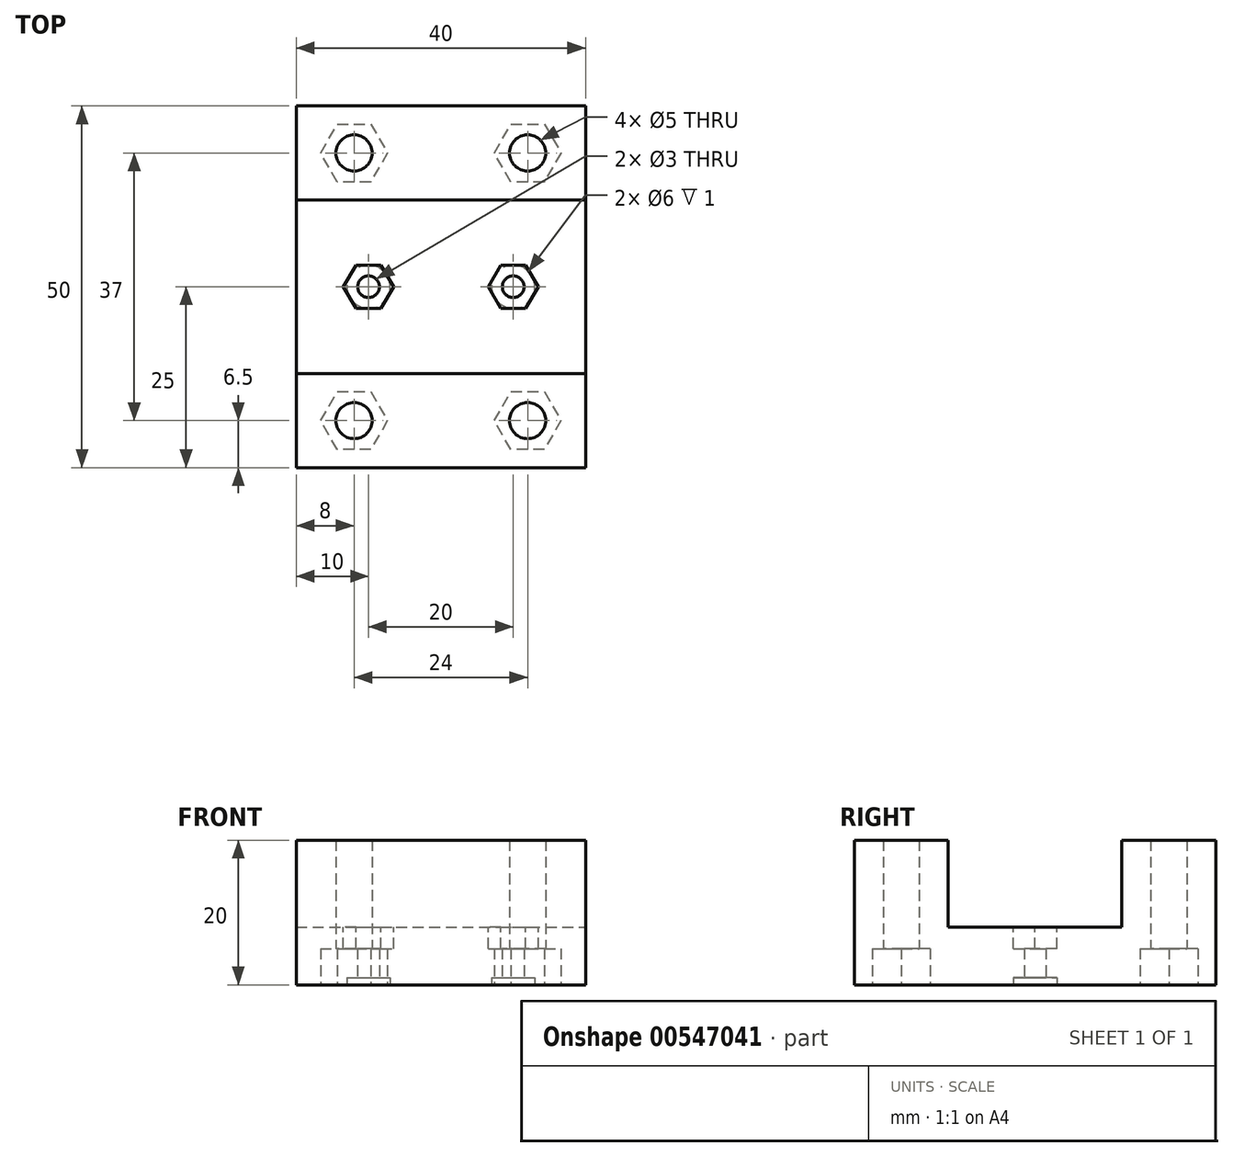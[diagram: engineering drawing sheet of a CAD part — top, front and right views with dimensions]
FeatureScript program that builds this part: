
annotation { "Feature Type Name" : "Feature", "Feature Type Description" : "" }
export const myFeature = defineFeature(function(context is Context, id is Id, definition is map)
    precondition{}
    {
        {
            var Q0;
            Q0=qCreatedBy(makeId("Top.planeOp"),FACE);
            var sketch = newSketch(context, id + "F0", { "sketchPlane" : qUnion([Q0])});
            skLineSegment(sketch, "E0.bottom", {"start": v(-40, 50) * mm, "end": v(0, 50) * mm});
            skLineSegment(sketch, "E0.top", {"start": v(-40, 0) * mm, "end": v(0, 0) * mm});
            skLineSegment(sketch, "E0.left", {"start": v(-40, 50) * mm, "end": v(-40, 0) * mm});
            skLineSegment(sketch, "E0.right", {"start": v(0, 50) * mm, "end": v(0, 0) * mm});
            skLineSegment(sketch, "E1", {"start": v(-40, 37) * mm, "end": v(0, 37) * mm});
            skLineSegment(sketch, "E2", {"start": v(-40, 13) * mm, "end": v(0, 13) * mm});
            skPoint(sketch, "E3", {"position": v(-8, 6.5) * mm});
            skPoint(sketch, "E4", {"position": v(-32, 43.5) * mm});
            skPoint(sketch, "E5", {"position": v(-32, 6.5) * mm});
            skPoint(sketch, "E6", {"position": v(-8, 43.5) * mm});
            skSolve(sketch);
        }
        {
            var Q0;
            {var subQ0=sQuery(id+"F0.wireOp",EDGE,"E1");Q0=makeQuery(id+"F0.imprint","IMPRINT",FACE,{"disambiguationData":[TD([[makeQuery(id+"F0.imprint","IMPRINT",EDGE,{"derivedFrom":subQ0}),-1.0]])]});}
            extrude(context, id + "F1", {"entities" : qUnion([Q0]), "depth" : 8 * mm, "offsetDistance" : 25 * mm});
        }
        {
            var Q0;
            {var subQ0=sQuery(id+"F0.wireOp",EDGE,"E0.bottom");Q0=makeQuery(id+"F0.imprint","IMPRINT",FACE,{"disambiguationData":[TD([[makeQuery(id+"F0.imprint","IMPRINT",EDGE,{"derivedFrom":subQ0}),-1.0]])]});}
            var Q1;
            {var subQ0=sQuery(id+"F0.wireOp",EDGE,"E0.top");Q1=makeQuery(id+"F0.imprint","IMPRINT",FACE,{"disambiguationData":[TD([[makeQuery(id+"F0.imprint","IMPRINT",EDGE,{"derivedFrom":subQ0}),1.0]])]});}
            extrude(context, id + "F2", {"entities" : qUnion([Q0, Q1]), "operationType" : NewBodyOperationType.ADD, "depth" : 20 * mm, "offsetDistance" : 25 * mm});
        }
        {
            var Q0;
            Q0=sQuery(id+"F0.wireOp",VERTEX,"E6");
            var Q1;
            Q1=sQuery(id+"F0.wireOp",VERTEX,"E4");
            var Q2;
            Q2=sQuery(id+"F0.wireOp",VERTEX,"E5");
            var Q3;
            Q3=sQuery(id+"F0.wireOp",VERTEX,"E3");
            var Q4;
            Q4=makeQuery(id+"F1.opExtrude","SWEPT_BODY",BODY,{"disambiguationData":[OSD([sQuery(id+"F0.wireOp",EDGE,"E0.left"),sQuery(id+"F0.wireOp",EDGE,"E0.right"),sQuery(id+"F0.wireOp",EDGE,"E1"),sQuery(id+"F0.wireOp",EDGE,"E2")])]});
            hole(context, id + "F3", {"style" : HoleStyle.SIMPLE, "endStyle" : HoleEndStyle.THROUGH, "oppositeDirection" : true, "holeDiameter" : 5 * mm, "isTappedThrough" : true, "tappedDepth" : 12 * mm, "tapClearance" : 3, "startFromSketch" : true, "locations" : qUnion([Q0, Q1, Q2, Q3]), "scope" : qUnion([Q4])});
        }
        {
            var Q0;
            {var subQ0=sQuery(id+"F0.wireOp",EDGE,"E0.top");Q0=makeQuery(id+"F0.imprint","IMPRINT",FACE,{"disambiguationData":[TD([[makeQuery(id+"F0.imprint","IMPRINT",EDGE,{"derivedFrom":subQ0}),1.0]])]});}
            var sketch = newSketch(context, id + "F4", { "sketchPlane" : qUnion([Q0])});
            skLineSegment(sketch, "E7", {"start": v(-10.3, 47.5) * mm, "end": v(-5.7, 47.5) * mm});
            skLineSegment(sketch, "E8", {"start": v(-5.7, 47.5) * mm, "end": v(-3.38, 43.5) * mm});
            skLineSegment(sketch, "E9", {"start": v(-3.38, 43.5) * mm, "end": v(-5.7, 39.5) * mm});
            skLineSegment(sketch, "E10", {"start": v(-5.7, 39.5) * mm, "end": v(-10.3, 39.5) * mm});
            skLineSegment(sketch, "E11", {"start": v(-10.3, 39.5) * mm, "end": v(-12.62, 43.5) * mm});
            skLineSegment(sketch, "E12", {"start": v(-12.62, 43.5) * mm, "end": v(-10.3, 47.5) * mm});
            skCircle(sketch, "E13", {"center": v(-8, 43.5) * mm, "radius": 4.62 * mm});
            skLineSegment(sketch, "E14", {"start": v(-10.3, 10.5) * mm, "end": v(-5.7, 10.5) * mm});
            skLineSegment(sketch, "E15", {"start": v(-5.7, 10.5) * mm, "end": v(-3.38, 6.5) * mm});
            skLineSegment(sketch, "E16", {"start": v(-3.38, 6.5) * mm, "end": v(-5.7, 2.5) * mm});
            skLineSegment(sketch, "E17", {"start": v(-5.7, 2.5) * mm, "end": v(-10.3, 2.5) * mm});
            skLineSegment(sketch, "E18", {"start": v(-10.3, 2.5) * mm, "end": v(-12.62, 6.5) * mm});
            skLineSegment(sketch, "E19", {"start": v(-12.62, 6.5) * mm, "end": v(-10.3, 10.5) * mm});
            skCircle(sketch, "E20", {"center": v(-8, 6.5) * mm, "radius": 4.62 * mm});
            skLineSegment(sketch, "E21", {"start": v(-34.3, 10.5) * mm, "end": v(-29.7, 10.5) * mm});
            skLineSegment(sketch, "E22", {"start": v(-29.7, 10.5) * mm, "end": v(-27.38, 6.5) * mm});
            skLineSegment(sketch, "E23", {"start": v(-27.38, 6.5) * mm, "end": v(-29.7, 2.5) * mm});
            skLineSegment(sketch, "E24", {"start": v(-29.7, 2.5) * mm, "end": v(-34.3, 2.5) * mm});
            skLineSegment(sketch, "E25", {"start": v(-34.3, 2.5) * mm, "end": v(-36.62, 6.5) * mm});
            skLineSegment(sketch, "E26", {"start": v(-36.62, 6.5) * mm, "end": v(-34.3, 10.5) * mm});
            skCircle(sketch, "E27", {"center": v(-32, 6.5) * mm, "radius": 4.62 * mm});
            skLineSegment(sketch, "E28", {"start": v(-34.3, 47.5) * mm, "end": v(-29.7, 47.5) * mm});
            skLineSegment(sketch, "E29", {"start": v(-29.7, 47.5) * mm, "end": v(-27.38, 43.5) * mm});
            skLineSegment(sketch, "E30", {"start": v(-27.38, 43.5) * mm, "end": v(-29.7, 39.5) * mm});
            skLineSegment(sketch, "E31", {"start": v(-29.7, 39.5) * mm, "end": v(-34.3, 39.5) * mm});
            skLineSegment(sketch, "E32", {"start": v(-34.3, 39.5) * mm, "end": v(-36.62, 43.5) * mm});
            skLineSegment(sketch, "E33", {"start": v(-36.62, 43.5) * mm, "end": v(-34.3, 47.5) * mm});
            skCircle(sketch, "E34", {"center": v(-32, 43.5) * mm, "radius": 4.62 * mm});
            skSolve(sketch);
        }
        {
            var Q0;
            Q0=makeQuery(id+"F4.imprint","IMPRINT",FACE,{"disambiguationData":[TD([[makeQuery(id+"F4.imprint","IMPRINT",EDGE,{"derivedFrom":sQuery(id+"F4.wireOp",EDGE,"E21")}),-1.0]])]});
            var Q1;
            Q1=makeQuery(id+"F4.imprint","IMPRINT",FACE,{"disambiguationData":[TD([[makeQuery(id+"F4.imprint","IMPRINT",EDGE,{"derivedFrom":sQuery(id+"F4.wireOp",EDGE,"E14")}),-1.0]])]});
            var Q2;
            Q2=makeQuery(id+"F4.imprint","IMPRINT",FACE,{"disambiguationData":[TD([[makeQuery(id+"F4.imprint","IMPRINT",EDGE,{"derivedFrom":sQuery(id+"F4.wireOp",EDGE,"E7")}),-1.0]])]});
            var Q3;
            Q3=makeQuery(id+"F4.imprint","IMPRINT",FACE,{"disambiguationData":[TD([[makeQuery(id+"F4.imprint","IMPRINT",EDGE,{"derivedFrom":sQuery(id+"F4.wireOp",EDGE,"E28")}),-1.0]])]});
            extrude(context, id + "F5", {"entities" : qUnion([Q0, Q1, Q2, Q3]), "operationType" : NewBodyOperationType.REMOVE, "depth" : 5 * mm, "offsetDistance" : 25 * mm});
        }
        {
            var Q0;
            {var subQ0=sQuery(id+"F0.wireOp",EDGE,"E1");Q0=makeQuery(id+"F0.imprint","IMPRINT",FACE,{"disambiguationData":[TD([[makeQuery(id+"F0.imprint","IMPRINT",EDGE,{"derivedFrom":subQ0}),-1.0]])]});}
            var sketch = newSketch(context, id + "F6", { "sketchPlane" : qUnion([Q0])});
            skPoint(sketch, "E35", {"position": v(-30, 25) * mm});
            skPoint(sketch, "E36", {"position": v(-10, 25) * mm});
            skSolve(sketch);
        }
        {
            var Q0;
            Q0=sQuery(id+"F6.wireOp",VERTEX,"E35");
            var Q1;
            Q1=sQuery(id+"F6.wireOp",VERTEX,"E36");
            var Q2;
            Q2=makeQuery(id+"F1.opExtrude","SWEPT_BODY",BODY,{"disambiguationData":[OSD([sQuery(id+"F0.wireOp",EDGE,"E0.left"),sQuery(id+"F0.wireOp",EDGE,"E0.right"),sQuery(id+"F0.wireOp",EDGE,"E1"),sQuery(id+"F0.wireOp",EDGE,"E2")])]});
            hole(context, id + "F7", {"style" : HoleStyle.C_BORE, "endStyle" : HoleEndStyle.THROUGH, "oppositeDirection" : true, "holeDiameter" : 3 * mm, "cBoreDiameter" : 6 * mm, "cBoreDepth" : 1 * mm, "isTappedThrough" : true, "tappedDepth" : 12 * mm, "tapClearance" : 3, "startFromSketch" : true, "locations" : qUnion([Q0, Q1]), "scope" : qUnion([Q2])});
        }
        {
            var Q0;
            Q0=makeQuery(id+"F1.opExtrude","CAP_FACE",FACE,{"disambiguationData":[OSD([sQuery(id+"F0.wireOp",EDGE,"E0.left"),sQuery(id+"F0.wireOp",EDGE,"E0.right"),sQuery(id+"F0.wireOp",EDGE,"E1"),sQuery(id+"F0.wireOp",EDGE,"E2")])],"isStart":false});
            var sketch = newSketch(context, id + "F8", { "sketchPlane" : qUnion([Q0])});
            skLineSegment(sketch, "E37", {"start": v(-11.73, 28) * mm, "end": v(-8.27, 28) * mm});
            skLineSegment(sketch, "E38", {"start": v(-8.27, 28) * mm, "end": v(-6.54, 25) * mm});
            skLineSegment(sketch, "E39", {"start": v(-6.54, 25) * mm, "end": v(-8.27, 22) * mm});
            skLineSegment(sketch, "E40", {"start": v(-8.27, 22) * mm, "end": v(-11.73, 22) * mm});
            skLineSegment(sketch, "E41", {"start": v(-11.73, 22) * mm, "end": v(-13.46, 25) * mm});
            skLineSegment(sketch, "E42", {"start": v(-13.46, 25) * mm, "end": v(-11.73, 28) * mm});
            skCircle(sketch, "E43", {"center": v(-10, 25) * mm, "radius": 3.46 * mm});
            skLineSegment(sketch, "E44", {"start": v(-31.73, 28) * mm, "end": v(-28.27, 28) * mm});
            skLineSegment(sketch, "E45", {"start": v(-28.27, 28) * mm, "end": v(-26.54, 25) * mm});
            skLineSegment(sketch, "E46", {"start": v(-26.54, 25) * mm, "end": v(-28.27, 22) * mm});
            skLineSegment(sketch, "E47", {"start": v(-28.27, 22) * mm, "end": v(-31.73, 22) * mm});
            skLineSegment(sketch, "E48", {"start": v(-31.73, 22) * mm, "end": v(-33.46, 25) * mm});
            skLineSegment(sketch, "E49", {"start": v(-33.46, 25) * mm, "end": v(-31.73, 28) * mm});
            skCircle(sketch, "E50", {"center": v(-30, 25) * mm, "radius": 3.46 * mm});
            skSolve(sketch);
        }
        {
            var Q0;
            Q0=makeQuery(id+"F8.imprint","IMPRINT",FACE,{"disambiguationData":[TD([[makeQuery(id+"F8.imprint","IMPRINT",EDGE,{"derivedFrom":sQuery(id+"F8.wireOp",EDGE,"E37")}),-1.0]])]});
            var Q1;
            Q1=makeQuery(id+"F8.imprint","IMPRINT",FACE,{"disambiguationData":[TD([[makeQuery(id+"F8.imprint","IMPRINT",EDGE,{"derivedFrom":sQuery(id+"F8.wireOp",EDGE,"E44")}),-1.0]])]});
            extrude(context, id + "F9", {"entities" : qUnion([Q0, Q1]), "operationType" : NewBodyOperationType.REMOVE, "oppositeDirection" : true, "depth" : 3 * mm, "offsetDistance" : 25 * mm});
        }
    });
